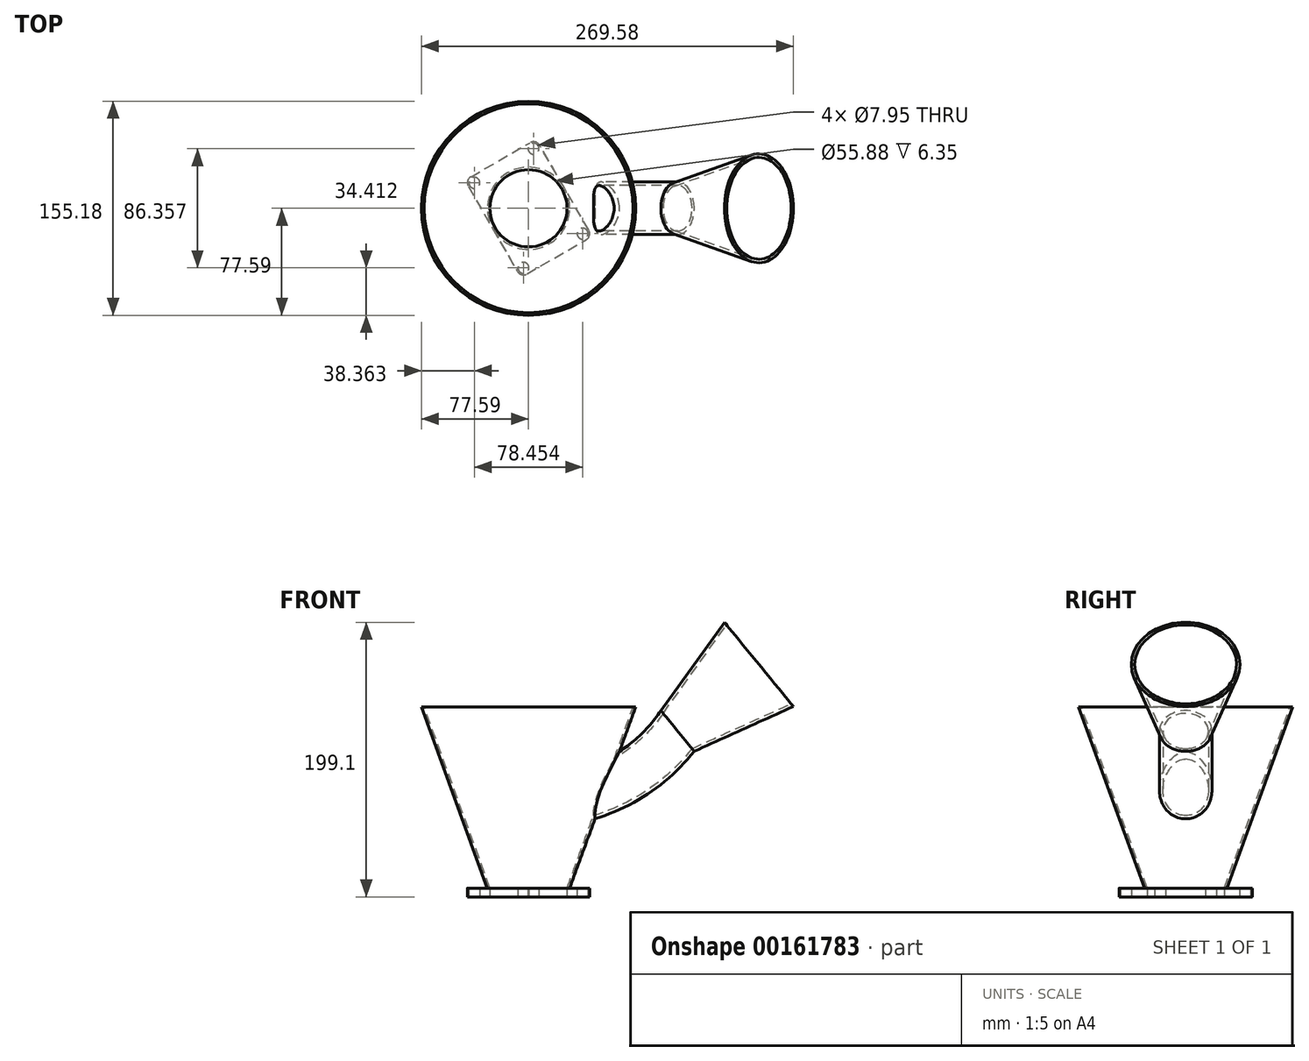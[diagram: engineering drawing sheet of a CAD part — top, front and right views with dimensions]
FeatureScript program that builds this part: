
annotation { "Feature Type Name" : "Feature", "Feature Type Description" : "" }
export const myFeature = defineFeature(function(context is Context, id is Id, definition is map)
    precondition{}
    {
        {
            var Q0;
            Q0=qCreatedBy(makeId("Top.planeOp"),FACE);
            var sketch = newSketch(context, id + "F0", { "sketchPlane" : qUnion([Q0])});
            skLineSegment(sketch, "E0", {"start": v(-43.63, 15.87) * mm, "end": v(-8.07, -45.72) * mm});
            skLineSegment(sketch, "E1", {"start": v(-1.13, -47.58) * mm, "end": v(41.77, -22.81) * mm});
            skLineSegment(sketch, "E2", {"start": v(43.63, -15.87) * mm, "end": v(8.07, 45.72) * mm});
            skLineSegment(sketch, "E3", {"start": v(-41.77, 22.81) * mm, "end": v(1.13, 47.58) * mm});
            skCircle(sketch, "E4", {"center": v(0, 0) * mm, "radius": 27.94 * mm});
            skCircle(sketch, "E5", {"center": v(-39.23, 18.41) * mm, "radius": 3.98 * mm});
            skCircle(sketch, "E6", {"center": v(3.67, 43.18) * mm, "radius": 3.98 * mm});
            skCircle(sketch, "E7", {"center": v(39.23, -18.41) * mm, "radius": 3.98 * mm});
            skCircle(sketch, "E8", {"center": v(-3.67, -43.18) * mm, "radius": 3.98 * mm});
            skPoint(sketch, "E9.visualSharp", {"position": v(-46.17, 20.27) * mm});
            skArc(sketch, "E9.filletArc", {"start": v(-41.77, 22.81) * mm, "mid": v(-44.13, 19.73) * mm, "end": v(-43.63, 15.87) * mm});
            skPoint(sketch, "E10.visualSharp", {"position": v(5.53, 50.12) * mm});
            skArc(sketch, "E10.filletArc", {"start": v(8.07, 45.72) * mm, "mid": v(4.98, 48.09) * mm, "end": v(1.13, 47.58) * mm});
            skPoint(sketch, "E11.visualSharp", {"position": v(46.17, -20.27) * mm});
            skArc(sketch, "E11.filletArc", {"start": v(41.77, -22.81) * mm, "mid": v(44.13, -19.73) * mm, "end": v(43.63, -15.87) * mm});
            skPoint(sketch, "E12.visualSharp", {"position": v(-5.53, -50.12) * mm});
            skArc(sketch, "E12.filletArc", {"start": v(-8.07, -45.72) * mm, "mid": v(-4.98, -48.09) * mm, "end": v(-1.13, -47.58) * mm});
            skSolve(sketch);
        }
        {
            var Q0;
            Q0 = qSketchRegion(id + "F0", true);
            extrude(context, id + "F1", {"entities" : qUnion([Q0]), "depth" : 6.35 * mm});
        }
        {
            var Q0;
            Q0=makeQuery(id+"F1.opExtrude","CAP_FACE",FACE,{"disambiguationData":[OSD([sQuery(id+"F0.wireOp",EDGE,"E0"),sQuery(id+"F0.wireOp",EDGE,"E1"),sQuery(id+"F0.wireOp",EDGE,"E2"),sQuery(id+"F0.wireOp",EDGE,"E3"),sQuery(id+"F0.wireOp",EDGE,"E4"),sQuery(id+"F0.wireOp",EDGE,"E5"),sQuery(id+"F0.wireOp",EDGE,"E6"),sQuery(id+"F0.wireOp",EDGE,"E7"),sQuery(id+"F0.wireOp",EDGE,"E8"),sQuery(id+"F0.wireOp",EDGE,"E9.filletArc"),sQuery(id+"F0.wireOp",EDGE,"E10.filletArc"),sQuery(id+"F0.wireOp",EDGE,"E11.filletArc"),sQuery(id+"F0.wireOp",EDGE,"E12.filletArc")])],"isStart":false});
            var sketch = newSketch(context, id + "F2", { "sketchPlane" : qUnion([Q0])});
            skLineSegment(sketch, "E13.0", {"start": v(43.63, -15.87) * mm, "end": v(8.07, 45.72) * mm});
            skCircle(sketch, "E14", {"center": v(0, 0) * mm, "radius": 29.85 * mm});
            skSolve(sketch);
        }
        {
            var Q0;
            Q0 = qSketchRegion(id + "F2", true);
            extrude(context, id + "F3", {"entities" : qUnion([Q0]), "operationType" : NewBodyOperationType.ADD, "endBound" : BoundingType.THROUGH_ALL, "depth" : 152.4 * mm, "hasDraft" : true, "draftAngle" : 20 * degree});
        }
        {
            var Q0;
            Q0=qCreatedBy(makeId("Right.planeOp"),FACE);
            var sketch = newSketch(context, id + "F4", { "sketchPlane" : qUnion([Q0])});
            skCircle(sketch, "E15", {"center": v(0, 63.5) * mm, "radius": 19.05 * mm});
            skSolve(sketch);
        }
        {
            var Q0;
            Q0=qCreatedBy(makeId("Front.planeOp"),FACE);
            var sketch = newSketch(context, id + "F5", { "sketchPlane" : qUnion([Q0])});
            skPoint(sketch, "E16.0", {"position": v(0, 63.5) * mm});
            skLineSegment(sketch, "E17", {"start": v(0, 63.5) * mm, "end": v(37.07, 72.82) * mm});
            skArc(sketch, "E18", {"start": v(37.07, 72.82) * mm, "mid": v(76.66, 90.4) * mm, "end": v(108.03, 120.28) * mm});
            skSolve(sketch);
        }
        {
            var Q0;
            Q0 = qSketchRegion(id + "F4", true);
            var Q1;
            Q1 = qConstructionFilter(qBodyType(qCreatedBy(id + "F5" ,EDGE), BodyType.WIRE), ConstructionObject.NO);
            sweep(context, id + "F6", {"operationType" : NewBodyOperationType.ADD, "profiles" : qUnion([Q0]), "path" : qUnion([Q1])});
        }
        {
            var Q0;
            Q0=makeQuery(id+"F6.opSweep","CAP_FACE",FACE,{"disambiguationData":[OSD([sQuery(id+"F4.wireOp",EDGE,"E15"),sQuery(id+"F5.wireOp",VERTEX,"E18.end")])],"isStart":false});
            var sketch = newSketch(context, id + "F7", { "sketchPlane" : qUnion([Q0])});
            skCircle(sketch, "E19.0", {"center": v(0, 24.6) * mm, "radius": 19.05 * mm});
            skCircle(sketch, "E20.0", {"center": v(0, 24.6) * mm, "radius": 16.51 * mm});
            skSolve(sketch);
        }
        {
            var Q0;
            Q0=makeQuery(id+"F7.imprint","IMPRINT",FACE,{"disambiguationData":[TD([[makeQuery(id+"F7.imprint","IMPRINT",EDGE,{"derivedFrom":sQuery(id+"F7.wireOp",EDGE,"E20.0")}),1.0]])]});
            var Q1;
            Q1 = qConstructionFilter(qBodyType(qCreatedBy(id + "F5" ,EDGE), BodyType.WIRE), ConstructionObject.NO);
            sweep(context, id + "F8", {"operationType" : NewBodyOperationType.REMOVE, "profiles" : qUnion([Q0]), "path" : qUnion([Q1])});
        }
        {
            var Q0;
            Q0=makeQuery(id+"F2.imprint","IMPRINT",FACE,{"disambiguationData":[TD([[makeQuery(id+"F2.imprint","IMPRINT",EDGE,{"derivedFrom":makeQuery(id+"F1.opExtrude","CAP_EDGE",EDGE,{"disambiguationData":[OSD([sQuery(id+"F0.wireOp",EDGE,"E1")])],"isStart":false})}),1.0]])]});
            cPlane(context, id + "F9", {"entities" : qUnion([Q0]), "cplaneType" : CPlaneType.OFFSET, "offset" : 0 * mm, "width" : 152.4 * mm, "height" : 152.4 * mm});
        }
        {
            var Q0;
            Q0=qCreatedBy(id+"F9.planeOp",FACE);
            var sketch = newSketch(context, id + "F10", { "sketchPlane" : qUnion([Q0])});
            skCircle(sketch, "E21.0", {"center": v(0, 0) * mm, "radius": 27.94 * mm});
            skSolve(sketch);
        }
        {
            var Q0;
            Q0 = qSketchRegion(id + "F10", true);
            extrude(context, id + "F11", {"entities" : qUnion([Q0]), "operationType" : NewBodyOperationType.REMOVE, "depth" : 152.4 * mm, "hasDraft" : true, "draftAngle" : 20 * degree});
        }
        {
            var Q0;
            Q0=makeQuery(id+"F6.opSweep","CAP_FACE",FACE,{"disambiguationData":[OSD([sQuery(id+"F4.wireOp",EDGE,"E15"),sQuery(id+"F5.wireOp",VERTEX,"E18.end")])],"isStart":false});
            cPlane(context, id + "F12", {"entities" : qUnion([Q0]), "cplaneType" : CPlaneType.OFFSET, "offset" : 0 * mm, "width" : 152.4 * mm, "height" : 152.4 * mm});
        }
        {
            var Q0;
            Q0=qCreatedBy(id+"F12.planeOp",FACE);
            var sketch = newSketch(context, id + "F13", { "sketchPlane" : qUnion([Q0])});
            skCircle(sketch, "E22.0", {"center": v(0, 24.6) * mm, "radius": 19.05 * mm});
            skSolve(sketch);
        }
        {
            var Q0;
            Q0 = qSketchRegion(id + "F13", true);
            extrude(context, id + "F14", {"entities" : qUnion([Q0]), "operationType" : NewBodyOperationType.ADD, "depth" : 76.2 * mm, "hasDraft" : true, "draftAngle" : 15 * degree});
        }
        {
            var Q0;
            Q0=qCreatedBy(id+"F12.planeOp",FACE);
            var sketch = newSketch(context, id + "F15", { "sketchPlane" : qUnion([Q0])});
            skCircle(sketch, "E23.0", {"center": v(0, 24.6) * mm, "radius": 16.51 * mm});
            skSolve(sketch);
        }
        {
            var Q0;
            Q0 = qSketchRegion(id + "F15", true);
            extrude(context, id + "F16", {"entities" : qUnion([Q0]), "operationType" : NewBodyOperationType.REMOVE, "depth" : 76.2 * mm, "hasDraft" : true, "draftAngle" : 15 * degree});
        }
    });
